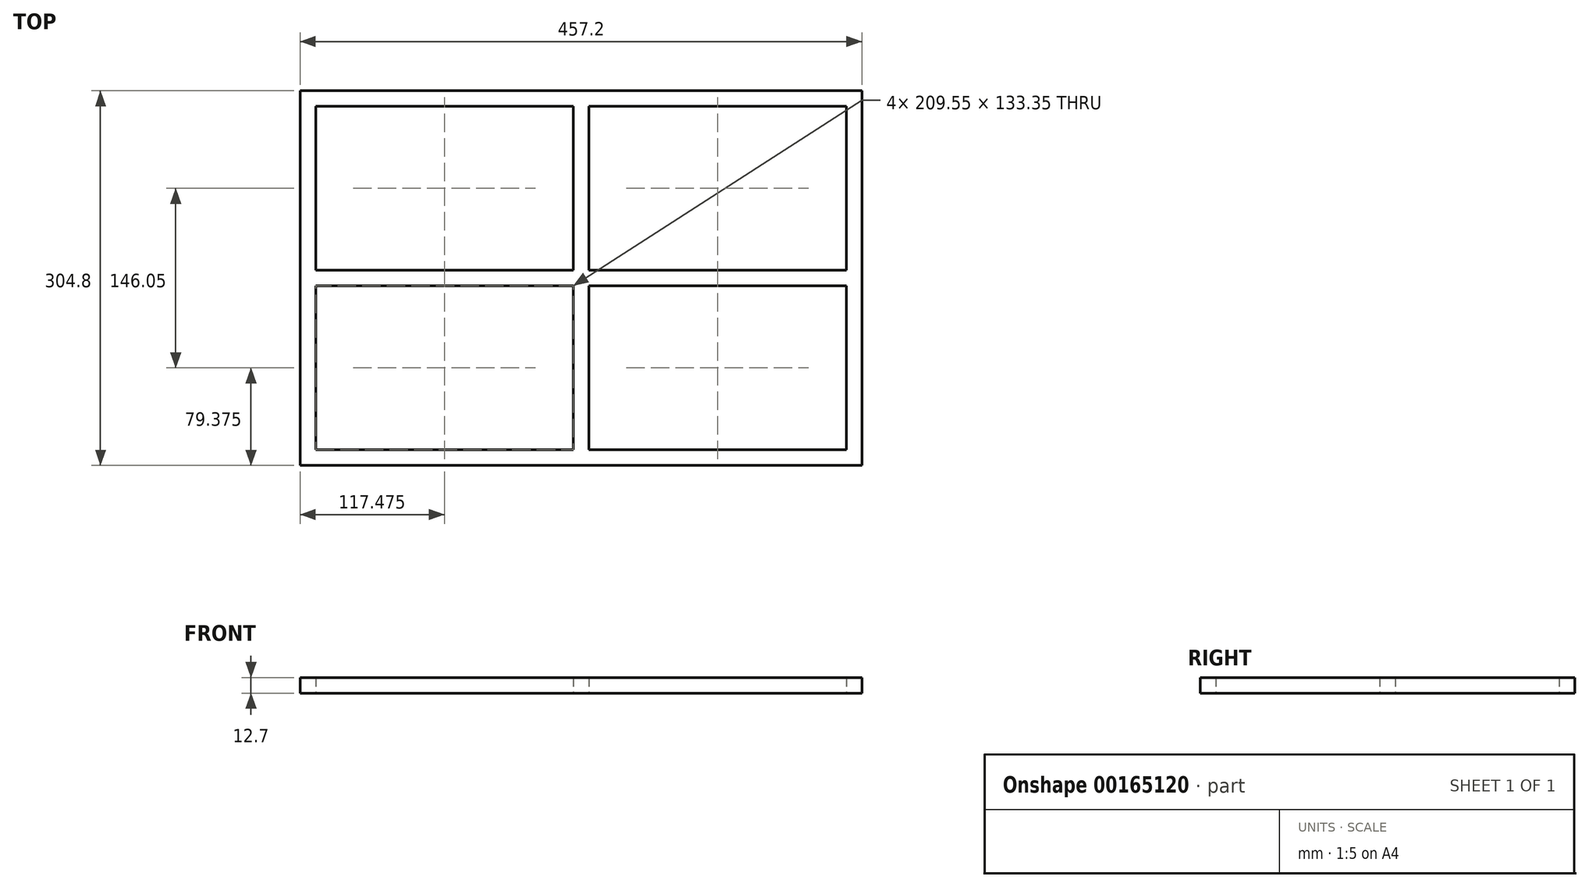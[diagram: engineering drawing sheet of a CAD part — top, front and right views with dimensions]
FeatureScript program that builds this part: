
annotation { "Feature Type Name" : "Feature", "Feature Type Description" : "" }
export const myFeature = defineFeature(function(context is Context, id is Id, definition is map)
    precondition{}
    {
        {
            var Q0;
            Q0=qCreatedBy(makeId("Top.planeOp"),FACE);
            var sketch = newSketch(context, id + "F0", { "sketchPlane" : qUnion([Q0])});
            skLineSegment(sketch, "E0.bottom", {"start": v(-6.35, 6.35) * mm, "end": v(6.35, 6.35) * mm, "construction": true});
            skLineSegment(sketch, "E0.top", {"start": v(-6.35, -6.35) * mm, "end": v(6.35, -6.35) * mm, "construction": true});
            skLineSegment(sketch, "E0.left", {"start": v(-6.35, 6.35) * mm, "end": v(-6.35, -6.35) * mm, "construction": true});
            skLineSegment(sketch, "E0.right", {"start": v(6.35, 6.35) * mm, "end": v(6.35, -6.35) * mm, "construction": true});
            skPoint(sketch, "E0.middle", {"position": v(0, 0) * mm});
            skLineSegment(sketch, "E1.bottom", {"start": v(-6.35, 6.35) * mm, "end": v(-215.9, 6.35) * mm});
            skLineSegment(sketch, "E1.top", {"start": v(-6.35, 139.7) * mm, "end": v(-215.9, 139.7) * mm});
            skLineSegment(sketch, "E1.left", {"start": v(-6.35, 6.35) * mm, "end": v(-6.35, 139.7) * mm});
            skLineSegment(sketch, "E1.right", {"start": v(-215.9, 6.35) * mm, "end": v(-215.9, 139.7) * mm});
            skLineSegment(sketch, "E2.bottom", {"start": v(6.35, 6.35) * mm, "end": v(215.9, 6.35) * mm});
            skLineSegment(sketch, "E2.top", {"start": v(6.35, 139.7) * mm, "end": v(215.9, 139.7) * mm});
            skLineSegment(sketch, "E2.left", {"start": v(6.35, 6.35) * mm, "end": v(6.35, 139.7) * mm});
            skLineSegment(sketch, "E2.right", {"start": v(215.9, 6.35) * mm, "end": v(215.9, 139.7) * mm});
            skLineSegment(sketch, "E3.bottom", {"start": v(6.35, -6.35) * mm, "end": v(215.9, -6.35) * mm});
            skLineSegment(sketch, "E3.top", {"start": v(6.35, -139.7) * mm, "end": v(215.9, -139.7) * mm});
            skLineSegment(sketch, "E3.left", {"start": v(6.35, -6.35) * mm, "end": v(6.35, -139.7) * mm});
            skLineSegment(sketch, "E3.right", {"start": v(215.9, -6.35) * mm, "end": v(215.9, -139.7) * mm});
            skLineSegment(sketch, "E4.bottom", {"start": v(-6.35, -6.35) * mm, "end": v(-215.9, -6.35) * mm});
            skLineSegment(sketch, "E4.top", {"start": v(-6.35, -139.7) * mm, "end": v(-215.9, -139.7) * mm});
            skLineSegment(sketch, "E4.left", {"start": v(-6.35, -6.35) * mm, "end": v(-6.35, -139.7) * mm});
            skLineSegment(sketch, "E4.right", {"start": v(-215.9, -6.35) * mm, "end": v(-215.9, -139.7) * mm});
            skLineSegment(sketch, "E5.bottom", {"start": v(228.6, 152.4) * mm, "end": v(-228.6, 152.4) * mm});
            skLineSegment(sketch, "E5.top", {"start": v(228.6, -152.4) * mm, "end": v(-228.6, -152.4) * mm});
            skLineSegment(sketch, "E5.left", {"start": v(228.6, 152.4) * mm, "end": v(228.6, -152.4) * mm});
            skLineSegment(sketch, "E5.right", {"start": v(-228.6, 152.4) * mm, "end": v(-228.6, -152.4) * mm});
            skLineSegment(sketch, "E6", {"start": v(215.9, 139.7) * mm, "end": v(228.6, 139.7) * mm, "construction": true});
            skLineSegment(sketch, "E7", {"start": v(215.9, 139.7) * mm, "end": v(215.9, 152.4) * mm, "construction": true});
            skSolve(sketch);
        }
        {
            var Q0;
            Q0 = qSketchRegion(id + "F0", true);
            extrude(context, id + "F1", {"entities" : qUnion([Q0]), "depth" : 12.7 * mm});
        }
    });
